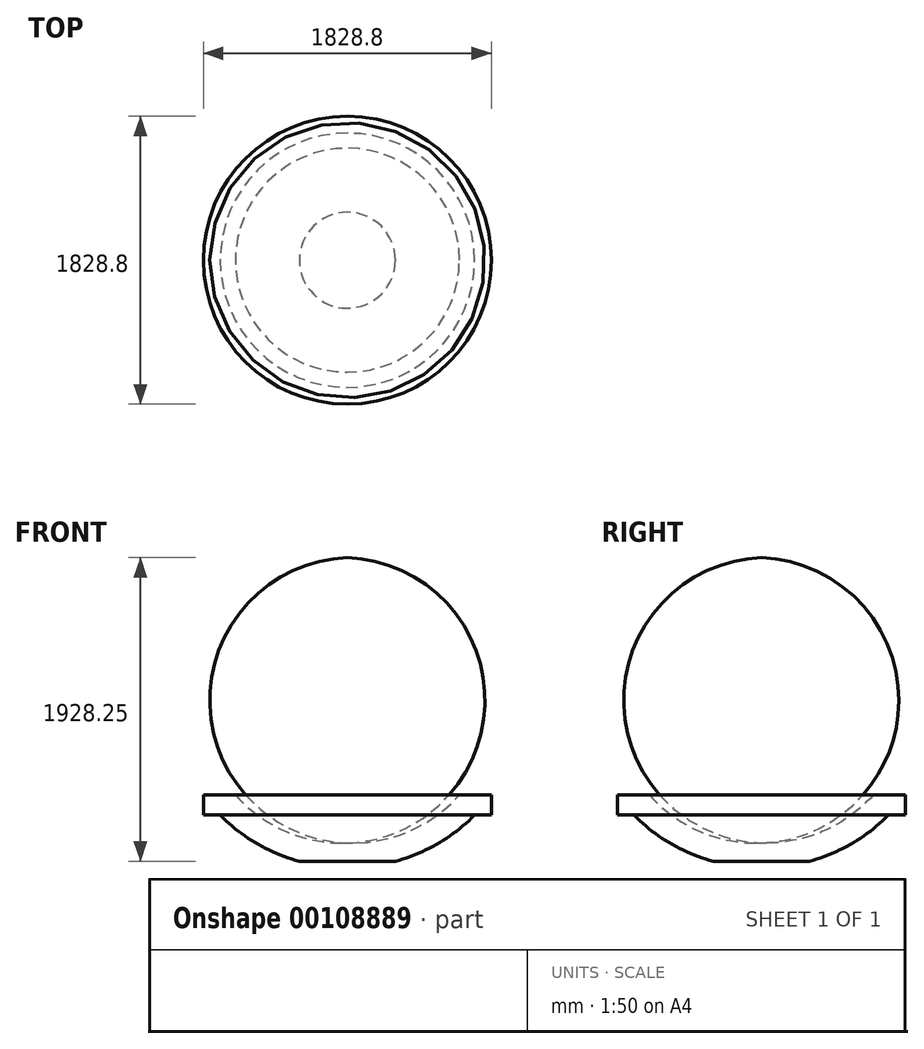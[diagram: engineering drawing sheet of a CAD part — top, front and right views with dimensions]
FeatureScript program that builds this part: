
annotation { "Feature Type Name" : "Feature", "Feature Type Description" : "" }
export const myFeature = defineFeature(function(context is Context, id is Id, definition is map)
    precondition{}
    {
        {
            var Q0;
            Q0=qCreatedBy(makeId("Front.planeOp"),FACE);
            var sketch = newSketch(context, id + "F0", { "sketchPlane" : qUnion([Q0])});
            skLineSegment(sketch, "E0", {"start": v(0, -304.8) * mm, "end": v(0, -421.16) * mm});
            skLineSegment(sketch, "E1", {"start": v(711.2, 0) * mm, "end": v(914.4, 0) * mm});
            skArc(sketch, "E2", {"start": v(0, -304.8) * mm, "mid": v(389.75, -232.1) * mm, "end": v(711.2, 0) * mm});
            skArc(sketch, "E3", {"start": v(304.8, -421.16) * mm, "mid": v(576.01, -308.59) * mm, "end": v(807.45, -127.85) * mm});
            skLineSegment(sketch, "E4", {"start": v(914.4, 0) * mm, "end": v(914.4, -127.85) * mm});
            skLineSegment(sketch, "E5", {"start": v(914.4, -127.85) * mm, "end": v(807.45, -127.85) * mm});
            skLineSegment(sketch, "E6", {"start": v(0, 133.1) * mm, "end": v(0, -421.16) * mm, "construction": true});
            skLineSegment(sketch, "E7", {"start": v(304.8, -240.02) * mm, "end": v(304.8, -546.88) * mm});
            skLineSegment(sketch, "E8", {"start": v(304.8, -421.16) * mm, "end": v(0, -421.16) * mm});
            skLineSegment(sketch, "E9.trimOffspring", {"start": v(0, -457.2) * mm, "end": v(0, -584.2) * mm, "construction": true});
            skSolve(sketch);
        }
        {
            var Q0;
            Q0 = qSketchRegion(id + "F0", true);
            var Q1;
            Q1=sQuery(id+"F0.wireOp",EDGE,"E6");
            revolve(context, id + "F1", {"entities" : qUnion([Q0]), "axis" : qUnion([Q1]), "revolveType" : RevolveType.FULL});
        }
    });
